# Revit family: Kessel 9820200D en
name_source: partatom
category: Sanitärinstallationen
revit_build: Autodesk Revit 2017 (Build: 20160225_1515(x64)
units: mm (PartAtom-declared; Revit-internal decimal feet)

## family parameters
Arbeitsebenenbasiert = Nein
Beim Laden mit Abzugskörper schneiden = Nein
Bemaßung runder Anschluss = Durchmesser verwenden
Gemeinsam genutzt = Nein
Immer vertikal = Ja
Raumberechnungspunkt = Nein
Teiletyp = Normal

## types (1)
- Kessel 9820200D en
    <1.010.00.2> Number of the part of the guideline = 98
    <1.010.00.3> Issue date (month) of the guideline = 200601
    <1.010.00.4> Manufacturer name = Kessel
    <1.010.00.5> Revision date of the file = 20190227
    <1.800.00.3> BS number = 001002000002006008011005015001002002005???01400018???
    <1.800.00.4> Comment field = Fettabscheider EasyClean Modular DIN 4040-100, NS 2, Standard, Klasse D
    <1.810.00.3> Manufacturer’s reference number = 98202/00D
    <1.810.00.4> DATANORM number = 98202/00D
    <1.810.00.6> GTIN number = 4026092027097
    <1.960/3L.00.8> Link (URL) = http://www.kessel.de
    <98.100.00.4> Area of application = Abscheideranlage für Fette
    <98.110.00.4> Product series = Fettabscheider EasyClean Modular
    <98.200.00.3> Installation of the separators (DIN 19901) = Erdeinbau
    <98.250.00.3> Disposal variant = Standard
    <98.260.00.3> Sludge trap content (liters) = 200
    <98.300.00.3> Separator content (liters) = 945
    <98.350.00.3> Fat storage (liters) = 80
    <98.360.00.3> Total volume (liters) = 1145
    <98.400.00.3> Layer thickness measurement (SonicControl) = nein
    <98.450.00.3> Inlet nominal diameter (DN) = 100
    <98.460.00.3> Outlet nominal diameter (DN) = 100
    <98.500.00.3> Nominal size (NS) = 2
    <98.700.00.4> Product name = Fettabscheider EasyClean Modular DIN 4040-100, NS 2, Standard, Klasse D
    CONNECTOR0_DIAMETER_dX_0r = 0 mm  [stored 0 ft]
    CONNECTOR0_dX_00 = 671 mm
    CONNECTOR0_dX_01 = 584 mm
    CONNECTOR0_ref_dX = 584 mm
    CONNECTOR0_ref_dZ = 1291 mm  [stored 4.23556 ft]
    CONNECTOR1_DIAMETER_dX_0r = 0 mm  [stored 0 ft]
    CONNECTOR1_dX_00 = 584 mm
    CONNECTOR1_dX_01 = 684 mm
    CONNECTOR1_ref_dX = 584 mm
    CONNECTOR1_ref_dZ = 1191 mm  [stored 3.90748 ft]
    Hersteller = Kessel
    Modell = 98202/00D
    URL = www.kessel.de

note: [stored X ft] marks values corroborated as IEEE doubles in the binary element streams (Revit-internal decimal feet)

## geometry (parser evidence)
native form markers: Sweep x2
no freeform markers — native parametric forms only
